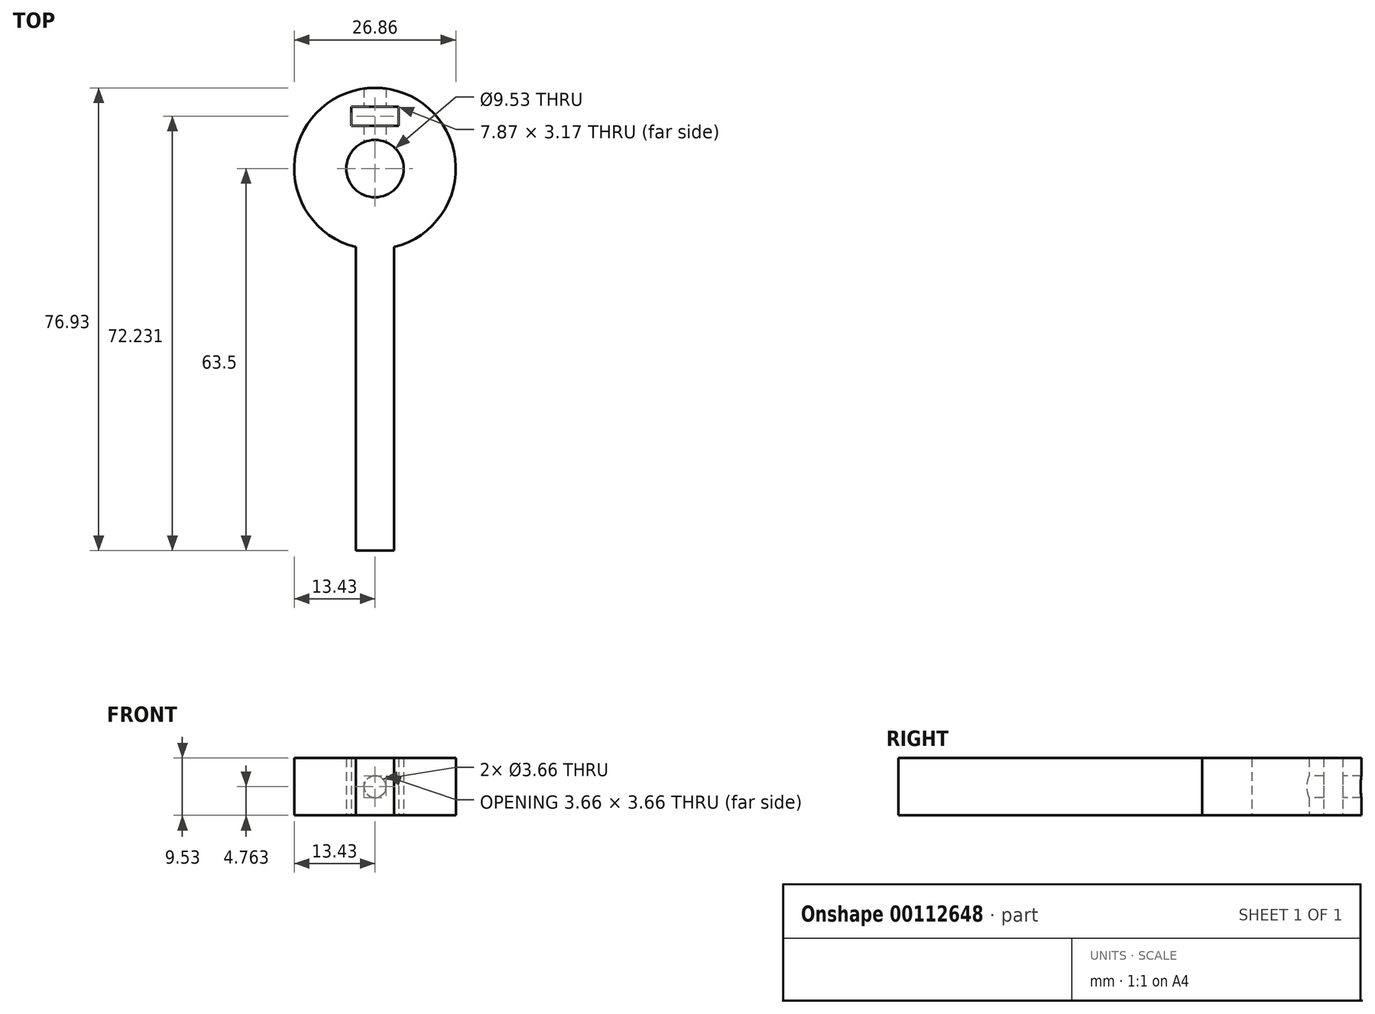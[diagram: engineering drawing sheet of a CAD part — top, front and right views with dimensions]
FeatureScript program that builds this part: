
annotation { "Feature Type Name" : "Feature", "Feature Type Description" : "" }
export const myFeature = defineFeature(function(context is Context, id is Id, definition is map)
    precondition{}
    {
        {
            var Q0;
            Q0=qCreatedBy(makeId("Top.planeOp"),FACE);
            var sketch = newSketch(context, id + "F0", { "sketchPlane" : qUnion([Q0])});
            skCircle(sketch, "E0", {"center": v(0, 0) * mm, "radius": 4.76 * mm});
            skLineSegment(sketch, "E1", {"start": v(0, 0) * mm, "end": v(0, 4.76) * mm, "construction": true});
            skLineSegment(sketch, "E2", {"start": v(0, 4.76) * mm, "end": v(0, 7.14) * mm, "construction": true});
            skLineSegment(sketch, "E3.bottom", {"start": v(-3.94, 7.14) * mm, "end": v(3.94, 7.14) * mm});
            skLineSegment(sketch, "E3.top", {"start": v(-3.94, 10.32) * mm, "end": v(3.94, 10.32) * mm});
            skLineSegment(sketch, "E3.left", {"start": v(-3.94, 7.14) * mm, "end": v(-3.94, 10.32) * mm});
            skLineSegment(sketch, "E3.right", {"start": v(3.94, 7.14) * mm, "end": v(3.94, 10.32) * mm});
            skCircle(sketch, "E4", {"center": v(3.94, 10.32) * mm, "radius": 2.38 * mm, "construction": true});
            skArc(sketch, "E5", {"start": v(3.17, -13.04) * mm, "mid": v(0, 13.43) * mm, "end": v(-3.17, -13.04) * mm});
            skLineSegment(sketch, "E6", {"start": v(0, 0) * mm, "end": v(0, -13.04) * mm, "construction": true});
            skLineSegment(sketch, "E7.bottom", {"start": v(-3.17, -13.04) * mm, "end": v(3.17, -13.04) * mm});
            skLineSegment(sketch, "E7.top", {"start": v(-3.17, -63.5) * mm, "end": v(3.17, -63.5) * mm});
            skLineSegment(sketch, "E7.left", {"start": v(-3.17, -13.04) * mm, "end": v(-3.17, -63.5) * mm});
            skLineSegment(sketch, "E7.right", {"start": v(3.18, -13.04) * mm, "end": v(3.18, -63.5) * mm});
            skSolve(sketch);
        }
        {
            var Q0;
            Q0 = qSketchRegion(id + "F0", true);
            extrude(context, id + "F1", {"entities" : qUnion([Q0]), "depth" : 9.52 * mm});
        }
        {
            var Q0;
            Q0=makeQuery(id+"F1.opExtrude","SWEPT_FACE",FACE,{"disambiguationData":[OSD([sQuery(id+"F0.wireOp",EDGE,"E3.top")])]});
            var sketch = newSketch(context, id + "F2", { "sketchPlane" : qUnion([Q0])});
            skLineSegment(sketch, "E8", {"start": v(0, 9.53) * mm, "end": v(0, 0) * mm, "construction": true});
            skCircle(sketch, "E9", {"center": v(0, 4.76) * mm, "radius": 1.83 * mm});
            skSolve(sketch);
        }
        {
            var Q0;
            Q0 = qSketchRegion(id + "F2", true);
            var Q1;
            Q1=makeQuery(id+"F1.opExtrude","SWEPT_FACE",FACE,{"disambiguationData":[OSD([sQuery(id+"F0.wireOp",EDGE,"E5")])]});
            var Q2;
            Q2=makeQuery(id+"F1.opExtrude","SWEPT_FACE",FACE,{"disambiguationData":[OSD([sQuery(id+"F0.wireOp",EDGE,"E0")])]});
            extrude(context, id + "F3", {"entities" : qUnion([Q0]), "operationType" : NewBodyOperationType.REMOVE, "endBound" : BoundingType.UP_TO_SURFACE, "oppositeDirection" : true, "endBoundEntityFace" : qUnion([Q1]), "depth" : 25.4 * mm, "hasSecondDirection" : true, "secondDirectionBound" : SecondDirectionBoundingType.UP_TO_SURFACE, "secondDirectionOppositeDirection" : false, "secondDirectionBoundEntityFace" : qUnion([Q2]), "secondDirectionDepth" : 25.4 * mm});
        }
    });
